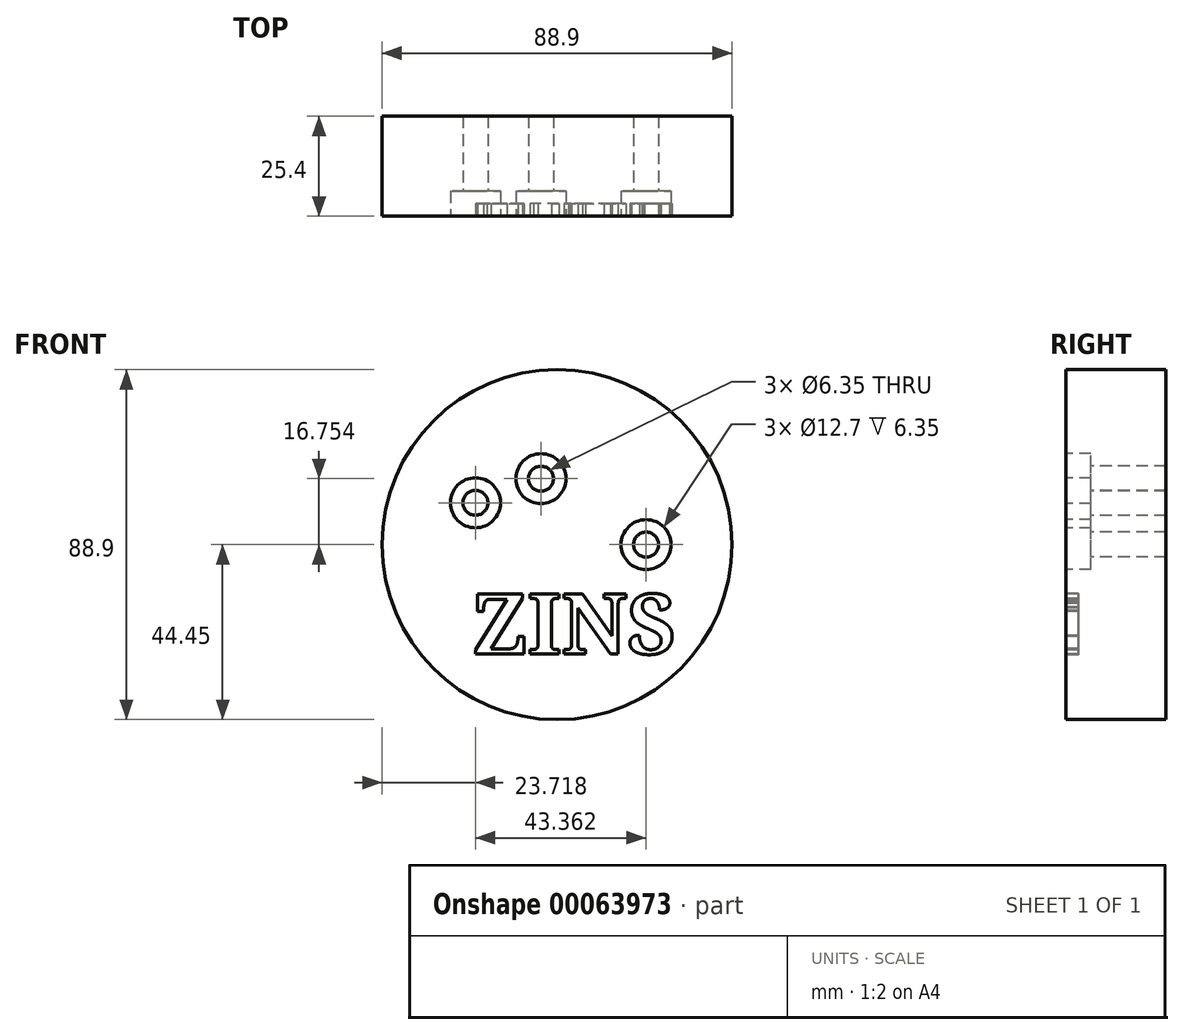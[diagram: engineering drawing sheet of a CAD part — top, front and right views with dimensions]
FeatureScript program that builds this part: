
annotation { "Feature Type Name" : "Feature", "Feature Type Description" : "" }
export const myFeature = defineFeature(function(context is Context, id is Id, definition is map)
    precondition{}
    {
        {
            var Q0;
            Q0=qCreatedBy(makeId("Front.planeOp"),FACE);
            var sketch = newSketch(context, id + "F0", { "sketchPlane" : qUnion([Q0])});
            skCircle(sketch, "E0", {"center": v(0, 0) * mm, "radius": 44.45 * mm});
            skSolve(sketch);
        }
        {
            var Q0;
            Q0=makeQuery(id+"F0.imprint","IMPRINT",FACE,{"disambiguationData":[TD([[makeQuery(id+"F0.imprint","IMPRINT",EDGE,{"derivedFrom":sQuery(id+"F0.wireOp",EDGE,"E0")}),1.0]])]});
            extrude(context, id + "F1", {"entities" : qUnion([Q0]), "depth" : 25.4 * mm});
        }
        {
            var Q0;
            Q0=makeQuery(id+"F1.opExtrude","CAP_FACE",FACE,{"disambiguationData":[OSD([sQuery(id+"F0.wireOp",EDGE,"E0")])],"isStart":false});
            var sketch = newSketch(context, id + "F2", { "sketchPlane" : qUnion([Q0])});
            skPoint(sketch, "E1", {"position": v(-4.09, 16.75) * mm});
            skPoint(sketch, "E2", {"position": v(-20.73, 10.64) * mm});
            skPoint(sketch, "E3", {"position": v(22.63, 0) * mm});
            skSolve(sketch);
        }
        {
            var Q0;
            Q0=sQuery(id+"F2.wireOp",VERTEX,"E2");
            var Q1;
            Q1=sQuery(id+"F2.wireOp",VERTEX,"E1");
            var Q2;
            Q2=sQuery(id+"F2.wireOp",VERTEX,"E3");
            var Q3;
            Q3=makeQuery(id+"F1.opExtrude","SWEPT_BODY",BODY,{"disambiguationData":[OSD([sQuery(id+"F0.wireOp",EDGE,"E0")])]});
            hole(context, id + "F3", {"style" : HoleStyle.C_BORE, "holeDiameter" : 6.35 * mm, "cBoreDiameter" : 12.7 * mm, "cBoreDepth" : 6.35 * mm, "endStyle" : HoleEndStyle.THROUGH, "locations" : qUnion([Q0, Q1, Q2]), "scope" : qUnion([Q3])});
        }
        {
            var Q0;
            Q0=makeQuery(id+"F1.opExtrude","CAP_FACE",FACE,{"disambiguationData":[OSD([sQuery(id+"F0.wireOp",EDGE,"E0")])],"isStart":false});
            var sketch = newSketch(context, id + "F4", { "sketchPlane" : qUnion([Q0])});
            skText(sketch, "E4", { "text": "ZINS", "fontName": "NotoSerif-Bold.ttf"});
            const initialGuessF4  = {"E4": [-0.02155, -0.02776, 1, 0, 0.0153]};
            skSetInitialGuess(sketch, initialGuessF4);
            skSolve(sketch);
        }
        {
            var Q0;
            Q0 = qSketchRegion(id + "F4", true);
            extrude(context, id + "F5", {"entities" : qUnion([Q0]), "operationType" : NewBodyOperationType.REMOVE, "oppositeDirection" : true, "depth" : 3.17 * mm});
        }
    });
